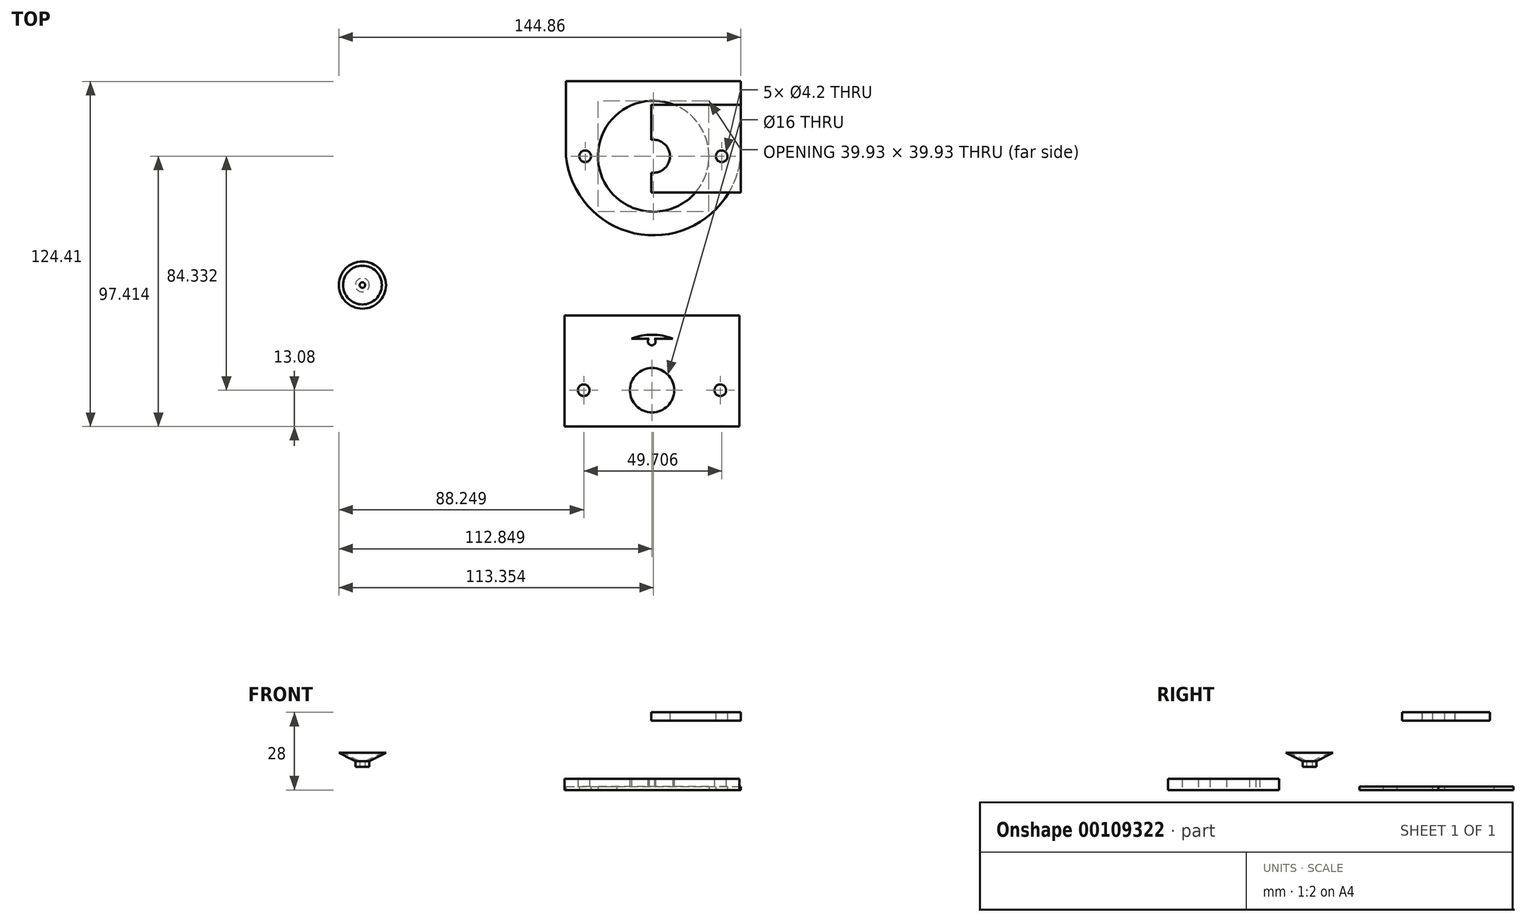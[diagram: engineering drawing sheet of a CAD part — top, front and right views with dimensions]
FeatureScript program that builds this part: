
annotation { "Feature Type Name" : "Feature", "Feature Type Description" : "" }
export const myFeature = defineFeature(function(context is Context, id is Id, definition is map)
    precondition{}
    {
        {
            var Q0;
            Q0=qCreatedBy(makeId("Top.planeOp"),FACE);
            var sketch = newSketch(context, id + "F0", { "sketchPlane" : qUnion([Q0])});
            skLineSegment(sketch, "E0.bottom", {"start": v(-41.15, 73.94) * mm, "end": v(21.85, 73.94) * mm});
            skLineSegment(sketch, "E0.top", {"start": v(-41.15, 23.94) * mm, "end": v(21.85, 23.94) * mm});
            skLineSegment(sketch, "E0.left", {"start": v(-41.15, 73.94) * mm, "end": v(-41.15, 23.94) * mm});
            skLineSegment(sketch, "E0.right", {"start": v(21.85, 73.94) * mm, "end": v(21.85, 23.94) * mm});
            skPoint(sketch, "E1", {"position": v(-9.65, 73.94) * mm});
            skPoint(sketch, "E2", {"position": v(-41.15, 48.94) * mm});
            skLineSegment(sketch, "E3", {"start": v(-41.15, 48.94) * mm, "end": v(-9.65, 48.94) * mm, "construction": true});
            skCircle(sketch, "E4", {"center": v(-9.65, 48.94) * mm, "radius": 5.95 * mm});
            skLineSegment(sketch, "E5.bottom", {"start": v(45.82, 73.43) * mm, "end": v(70.82, 73.43) * mm});
            skLineSegment(sketch, "E5.top", {"start": v(45.82, 31.43) * mm, "end": v(70.82, 31.43) * mm});
            skLineSegment(sketch, "E5.left", {"start": v(45.82, 73.43) * mm, "end": v(45.82, 31.43) * mm});
            skLineSegment(sketch, "E5.right", {"start": v(70.82, 73.43) * mm, "end": v(70.82, 31.43) * mm});
            skLineSegment(sketch, "E6", {"start": v(59.13, 31.43) * mm, "end": v(59.13, 43.93) * mm, "construction": true});
            skLineSegment(sketch, "E7", {"start": v(59.13, 43.93) * mm, "end": v(59.13, 46.43) * mm, "construction": true});
            skCircle(sketch, "E8", {"center": v(59.13, 46.43) * mm, "radius": 8 * mm});
            skLineSegment(sketch, "E9", {"start": v(59.02, 73.43) * mm, "end": v(59.02, 65.43) * mm, "construction": true});
            skPoint(sketch, "E10", {"position": v(56.32, 46.43) * mm});
            skLineSegment(sketch, "E11", {"start": v(56.32, 46.43) * mm, "end": v(59.13, 46.43) * mm, "construction": true});
            skLineSegment(sketch, "E12", {"start": v(59.02, 65.43) * mm, "end": v(59.02, 64.03) * mm, "construction": true});
            skCircle(sketch, "E13", {"center": v(59.02, 64.03) * mm, "radius": 1.4 * mm});
            skLineSegment(sketch, "E14", {"start": v(59.02, 64.03) * mm, "end": v(57.62, 64.03) * mm, "construction": true});
            skCircle(sketch, "E15", {"center": v(59.13, 46.43) * mm, "radius": 2.5 * mm});
            skCircle(sketch, "E16", {"center": v(59.13, 46.43) * mm, "radius": 20 * mm});
            skLineSegment(sketch, "E17", {"start": v(39.13, 46.43) * mm, "end": v(79.13, 46.43) * mm, "construction": true});
            skLineSegment(sketch, "E18", {"start": v(79.13, 46.43) * mm, "end": v(90.63, 46.43) * mm, "construction": true});
            skLineSegment(sketch, "E19", {"start": v(39.13, 46.43) * mm, "end": v(27.63, 46.43) * mm, "construction": true});
            skLineSegment(sketch, "E20", {"start": v(59.13, 31.43) * mm, "end": v(59.13, 26.43) * mm, "construction": true});
            skLineSegment(sketch, "E21", {"start": v(59.13, 26.43) * mm, "end": v(59.13, 17.93) * mm, "construction": true});
            skLineSegment(sketch, "E22", {"start": v(45.82, 73.43) * mm, "end": v(27.63, 73.43) * mm});
            skLineSegment(sketch, "E23", {"start": v(27.63, 73.43) * mm, "end": v(27.63, 46.43) * mm});
            skLineSegment(sketch, "E24", {"start": v(70.82, 73.43) * mm, "end": v(90.63, 73.43) * mm});
            skLineSegment(sketch, "E25", {"start": v(90.63, 73.43) * mm, "end": v(90.63, 46.43) * mm});
            skArc(sketch, "E26", {"start": v(27.63, 46.43) * mm, "mid": v(59.13, 17.93) * mm, "end": v(90.63, 46.43) * mm});
            skPoint(sketch, "E27", {"position": v(81.63, 46.43) * mm});
            skPoint(sketch, "E28", {"position": v(36.63, 46.43) * mm});
            skPoint(sketch, "E29", {"position": v(83.73, 46.43) * mm});
            skPoint(sketch, "E30", {"position": v(34.53, 46.43) * mm});
            skCircle(sketch, "E31", {"center": v(34.53, 46.43) * mm, "radius": 2.1 * mm});
            skCircle(sketch, "E32", {"center": v(83.73, 46.43) * mm, "radius": 2.1 * mm});
            skLineSegment(sketch, "E33", {"start": v(-9.65, 73.94) * mm, "end": v(-9.65, 23.94) * mm});
            skPoint(sketch, "E34", {"position": v(-9.65, 54.89) * mm});
            skLineSegment(sketch, "E35", {"start": v(27.63, 65) * mm, "end": v(90.63, 65) * mm});
            skPoint(sketch, "E35.endSnap0", {"position": v(90.63, 59.93) * mm});
            skLineSegment(sketch, "E36", {"start": v(27.63, 46.43) * mm, "end": v(27.63, 33.35) * mm});
            skLineSegment(sketch, "E37", {"start": v(27.63, 33.35) * mm, "end": v(90.63, 33.35) * mm});
            skLineSegment(sketch, "E38", {"start": v(90.63, 33.35) * mm, "end": v(90.63, 46.43) * mm});
            skSolve(sketch);
        }
        {
            var Q0;
            Q0=makeQuery(id+"F0.imprint","IMPRINT",FACE,{"disambiguationData":[TD([[makeQuery(id+"F0.imprint","IMPRINT",EDGE,{"derivedFrom":sQuery(id+"F0.wireOp",EDGE,"E32")}),-1.0]])]});
            var Q1;
            {var subQ0=sQuery(id+"F0.wireOp",EDGE,"E38");Q1=makeQuery(id+"F0.imprint","IMPRINT",FACE,{"disambiguationData":[TD([[makeQuery(id+"F0.imprint","IMPRINT",EDGE,{"derivedFrom":subQ0}),1.0]])]});}
            var Q2;
            {var subQ0=sQuery(id+"F0.wireOp",EDGE,"E24");Q2=makeQuery(id+"F0.imprint","IMPRINT",FACE,{"disambiguationData":[TD([[makeQuery(id+"F0.imprint","IMPRINT",EDGE,{"derivedFrom":subQ0}),-1.0]])]});}
            var Q3;
            Q3=makeQuery(id+"F0.imprint","IMPRINT",FACE,{"disambiguationData":[TD([[makeQuery(id+"F0.imprint","IMPRINT",EDGE,{"derivedFrom":sQuery(id+"F0.wireOp",EDGE,"E8")}),-1.0]])]});
            var Q4;
            Q4=makeQuery(id+"F0.imprint","IMPRINT",FACE,{"disambiguationData":[TD([[makeQuery(id+"F0.imprint","IMPRINT",EDGE,{"derivedFrom":sQuery(id+"F0.wireOp",EDGE,"E31")}),-1.0]])]});
            var Q5;
            {var subQ0=sQuery(id+"F0.wireOp",EDGE,"E22");Q5=makeQuery(id+"F0.imprint","IMPRINT",FACE,{"disambiguationData":[TD([[makeQuery(id+"F0.imprint","IMPRINT",EDGE,{"derivedFrom":subQ0}),1.0]])]});}
            var Q6;
            {var subQ0=sQuery(id+"F0.wireOp",EDGE,"E36");Q6=makeQuery(id+"F0.imprint","IMPRINT",FACE,{"disambiguationData":[TD([[makeQuery(id+"F0.imprint","IMPRINT",EDGE,{"derivedFrom":subQ0}),1.0]])]});}
            var Q7;
            {var subQ0=sQuery(id+"F0.wireOp",EDGE,"E16");var subQ1=sQuery(id+"F0.wireOp",EDGE,"E5.right");var subQ2=makeQuery(id+"F0.imprint","INTERSECT",VERTEX,{"derivedFrom":[subQ1,subQ0]});Q7=makeQuery(id+"F0.imprint","IMPRINT",FACE,{"disambiguationData":[TD([[makeQuery(id+"F0.imprint","IMPRINT",EDGE,{"disambiguationData":[TD([[subQ2,-1.0]])],"derivedFrom":subQ1}),1.0]])]});}
            var Q8;
            {var subQ0=sQuery(id+"F0.wireOp",EDGE,"E16");var subQ1=sQuery(id+"F0.wireOp",EDGE,"E5.left");var subQ2=makeQuery(id+"F0.imprint","INTERSECT",VERTEX,{"derivedFrom":[subQ1,subQ0]});Q8=makeQuery(id+"F0.imprint","IMPRINT",FACE,{"disambiguationData":[TD([[makeQuery(id+"F0.imprint","IMPRINT",EDGE,{"disambiguationData":[TD([[subQ2,-1.0]])],"derivedFrom":subQ1}),-1.0]])]});}
            var Q9;
            {var subQ0=sQuery(id+"F0.wireOp",EDGE,"E35");var subQ1=sQuery(id+"F0.wireOp",EDGE,"E5.right");var subQ2=makeQuery(id+"F0.imprint","INTERSECT",VERTEX,{"derivedFrom":[subQ1,subQ0]});Q9=makeQuery(id+"F0.imprint","IMPRINT",FACE,{"disambiguationData":[TD([[makeQuery(id+"F0.imprint","IMPRINT",EDGE,{"disambiguationData":[TD([[subQ2,-1.0]])],"derivedFrom":subQ1}),-1.0]])]});}
            var Q10;
            {var subQ0=sQuery(id+"F0.wireOp",EDGE,"E35");var subQ1=sQuery(id+"F0.wireOp",EDGE,"E13");var subQ2=makeQuery(id+"F0.imprint","INTERSECT",VERTEX,{"disambiguationData":[OD(0.0)],"derivedFrom":[subQ1,subQ0]});Q10=makeQuery(id+"F0.imprint","IMPRINT",FACE,{"disambiguationData":[TD([[makeQuery(id+"F0.imprint","IMPRINT",EDGE,{"disambiguationData":[TD([[subQ2,1.0]])],"derivedFrom":subQ1}),-1.0]])]});}
            var Q11;
            {var subQ6=sQuery(id+"F0.wireOp",EDGE,"E5.bottom");Q11=makeQuery(id+"F0.imprint","IMPRINT",FACE,{"disambiguationData":[TD([[makeQuery(id+"F0.imprint","IMPRINT",EDGE,{"derivedFrom":subQ6}),-1.0]])]});}
            var Q12;
            {var subQ0=sQuery(id+"F0.wireOp",EDGE,"E35");var subQ1=sQuery(id+"F0.wireOp",EDGE,"E5.left");var subQ2=makeQuery(id+"F0.imprint","INTERSECT",VERTEX,{"derivedFrom":[subQ1,subQ0]});Q12=makeQuery(id+"F0.imprint","IMPRINT",FACE,{"disambiguationData":[TD([[makeQuery(id+"F0.imprint","IMPRINT",EDGE,{"disambiguationData":[TD([[subQ2,-1.0]])],"derivedFrom":subQ1}),1.0]])]});}
            extrude(context, id + "F1", {"entities" : qUnion([Q0, Q1, Q2, Q3, Q4, Q5, Q6, Q7, Q8, Q9, Q10, Q11, Q12]), "depth" : 4 * mm});
        }
        {
            var Q0;
            Q0=makeQuery(id+"F1.opExtrude","SWEPT_BODY",BODY,{"disambiguationData":[OSD([sQuery(id+"F0.wireOp",EDGE,"E5.bottom"),sQuery(id+"F0.wireOp",EDGE,"E8"),sQuery(id+"F0.wireOp",EDGE,"E13"),sQuery(id+"F0.wireOp",EDGE,"E22"),sQuery(id+"F0.wireOp",EDGE,"E23"),sQuery(id+"F0.wireOp",EDGE,"E24"),sQuery(id+"F0.wireOp",EDGE,"E25"),sQuery(id+"F0.wireOp",EDGE,"E31"),sQuery(id+"F0.wireOp",EDGE,"E32"),sQuery(id+"F0.wireOp",EDGE,"E36"),sQuery(id+"F0.wireOp",EDGE,"E37"),sQuery(id+"F0.wireOp",EDGE,"E38")])]});
            transform(context, id + "F2", {"entities" : qUnion([Q0]), "transformType" : TransformType.TRANSLATION_3D, "dx" : -0.5 * mm, "dy" : -84.33 * mm, "dz" : 0 * mm, "makeCopy" : false});
        }
        {
            var Q0;
            Q0=makeQuery(id+"F0.imprint","IMPRINT",FACE,{"disambiguationData":[TD([[makeQuery(id+"F0.imprint","IMPRINT",EDGE,{"derivedFrom":sQuery(id+"F0.wireOp",EDGE,"E31")}),-1.0]])]});
            var Q1;
            Q1=makeQuery(id+"F0.imprint","IMPRINT",FACE,{"disambiguationData":[TD([[makeQuery(id+"F0.imprint","IMPRINT",EDGE,{"derivedFrom":sQuery(id+"F0.wireOp",EDGE,"E32")}),-1.0]])]});
            var Q2;
            {var subQ0=sQuery(id+"F0.wireOp",EDGE,"E24");Q2=makeQuery(id+"F0.imprint","IMPRINT",FACE,{"disambiguationData":[TD([[makeQuery(id+"F0.imprint","IMPRINT",EDGE,{"derivedFrom":subQ0}),-1.0]])]});}
            var Q3;
            {var subQ5=sQuery(id+"F0.wireOp",EDGE,"E5.bottom");Q3=makeQuery(id+"F0.imprint","IMPRINT",FACE,{"disambiguationData":[TD([[makeQuery(id+"F0.imprint","IMPRINT",EDGE,{"derivedFrom":subQ5}),-1.0]])]});}
            var Q4;
            {var subQ0=sQuery(id+"F0.wireOp",EDGE,"E22");Q4=makeQuery(id+"F0.imprint","IMPRINT",FACE,{"disambiguationData":[TD([[makeQuery(id+"F0.imprint","IMPRINT",EDGE,{"derivedFrom":subQ0}),1.0]])]});}
            var Q5;
            {var subQ0=sQuery(id+"F0.wireOp",EDGE,"E37");var subQ1=sQuery(id+"F0.wireOp",EDGE,"E16");var subQ2=makeQuery(id+"F0.imprint","INTERSECT",VERTEX,{"disambiguationData":[OD(0.0)],"derivedFrom":[subQ1,subQ0]});Q5=makeQuery(id+"F0.imprint","IMPRINT",FACE,{"disambiguationData":[TD([[makeQuery(id+"F0.imprint","IMPRINT",EDGE,{"disambiguationData":[TD([[subQ2,-1.0]])],"derivedFrom":subQ1}),-1.0]])]});}
            var Q6;
            {var subQ0=sQuery(id+"F0.wireOp",EDGE,"E35");var subQ1=sQuery(id+"F0.wireOp",EDGE,"E5.right");var subQ2=makeQuery(id+"F0.imprint","INTERSECT",VERTEX,{"derivedFrom":[subQ1,subQ0]});Q6=makeQuery(id+"F0.imprint","IMPRINT",FACE,{"disambiguationData":[TD([[makeQuery(id+"F0.imprint","IMPRINT",EDGE,{"disambiguationData":[TD([[subQ2,-1.0]])],"derivedFrom":subQ1}),-1.0]])]});}
            var Q7;
            {var subQ0=sQuery(id+"F0.wireOp",EDGE,"E35");var subQ1=sQuery(id+"F0.wireOp",EDGE,"E5.left");var subQ2=makeQuery(id+"F0.imprint","INTERSECT",VERTEX,{"derivedFrom":[subQ1,subQ0]});Q7=makeQuery(id+"F0.imprint","IMPRINT",FACE,{"disambiguationData":[TD([[makeQuery(id+"F0.imprint","IMPRINT",EDGE,{"disambiguationData":[TD([[subQ2,-1.0]])],"derivedFrom":subQ1}),1.0]])]});}
            extrude(context, id + "F3", {"entities" : qUnion([Q0, Q1, Q2, Q3, Q4, Q5, Q6, Q7]), "depth" : 1.2 * mm});
        }
        {
            var Q0;
            Q0=qCreatedBy(makeId("Top.planeOp"),FACE);
            cPlane(context, id + "F4", {"entities" : qUnion([Q0]), "cplaneType" : CPlaneType.OFFSET, "offset" : 25 * mm, "width" : 150 * mm, "height" : 150 * mm});
        }
        {
            var Q0;
            Q0=qCreatedBy(id+"F4.planeOp",FACE);
            var sketch = newSketch(context, id + "F5", { "sketchPlane" : qUnion([Q0])});
            skLineSegment(sketch, "E39.0", {"start": v(27.63, 65) * mm, "end": v(90.63, 65) * mm});
            skLineSegment(sketch, "E40.0", {"start": v(90.63, 73.43) * mm, "end": v(90.63, 46.43) * mm});
            skLineSegment(sketch, "E41.0", {"start": v(90.63, 33.35) * mm, "end": v(90.63, 46.43) * mm});
            skLineSegment(sketch, "E42.0", {"start": v(27.63, 33.35) * mm, "end": v(90.63, 33.35) * mm});
            skLineSegment(sketch, "E43.0", {"start": v(27.63, 46.43) * mm, "end": v(27.63, 33.35) * mm});
            skLineSegment(sketch, "E44.0", {"start": v(27.63, 73.43) * mm, "end": v(27.63, 46.43) * mm});
            skLineSegment(sketch, "E45.0", {"start": v(70.82, 73.43) * mm, "end": v(90.63, 73.43) * mm});
            skLineSegment(sketch, "E46.0", {"start": v(45.82, 73.43) * mm, "end": v(70.82, 73.43) * mm});
            skLineSegment(sketch, "E47.0", {"start": v(45.82, 73.43) * mm, "end": v(27.63, 73.43) * mm});
            skCircle(sketch, "E48.0", {"center": v(83.73, 46.43) * mm, "radius": 2.1 * mm});
            skCircle(sketch, "E49.0", {"center": v(34.53, 46.43) * mm, "radius": 2.1 * mm});
            skPoint(sketch, "E50", {"position": v(58.32, 73.43) * mm});
            skCircle(sketch, "E51", {"center": v(59.13, 46.43) * mm, "radius": 5.95 * mm});
            skLineSegment(sketch, "E52", {"start": v(58.32, 73.43) * mm, "end": v(58.32, 33.35) * mm});
            skSolve(sketch);
        }
        {
            var Q0;
            {var subQ1=sQuery(id+"F5.wireOp",EDGE,"E41.0");Q0=makeQuery(id+"F5.imprint","IMPRINT",FACE,{"disambiguationData":[TD([[makeQuery(id+"F5.imprint","IMPRINT",EDGE,{"derivedFrom":subQ1}),1.0]])]});}
            extrude(context, id + "F6", {"entities" : qUnion([Q0]), "depth" : 3 * mm});
        }
        {
            var Q0;
            Q0=qCreatedBy(makeId("Front.planeOp"),FACE);
            var sketch = newSketch(context, id + "F7", { "sketchPlane" : qUnion([Q0])});
            skLineSegment(sketch, "E53", {"start": v(-44.73, 8.38) * mm, "end": v(-44.73, 10.38) * mm});
            skLineSegment(sketch, "E54", {"start": v(-44.73, 10.38) * mm, "end": v(-38.73, 13.38) * mm});
            skLineSegment(sketch, "E55", {"start": v(-38.73, 13.38) * mm, "end": v(-37.23, 13.38) * mm});
            skLineSegment(sketch, "E56", {"start": v(-37.23, 13.38) * mm, "end": v(-43.23, 10.38) * mm});
            skLineSegment(sketch, "E57", {"start": v(-43.23, 10.38) * mm, "end": v(-43.23, 8.38) * mm});
            skLineSegment(sketch, "E58", {"start": v(-43.23, 8.38) * mm, "end": v(-44.73, 8.38) * mm});
            skLineSegment(sketch, "E59", {"start": v(-45.73, 6.83) * mm, "end": v(-45.73, 15.07) * mm});
            skSolve(sketch);
        }
        {
            var Q0;
            Q0=makeQuery(id+"F7.imprint","IMPRINT",FACE,{"disambiguationData":[TD([[makeQuery(id+"F7.imprint","IMPRINT",EDGE,{"derivedFrom":sQuery(id+"F7.wireOp",EDGE,"E53")}),-1.0]])]});
            var Q1;
            Q1=sQuery(id+"F7.wireOp",EDGE,"E59");
            revolve(context, id + "F8", {"entities" : qUnion([Q0]), "axis" : qUnion([Q1]), "revolveType" : RevolveType.FULL});
        }
    });
